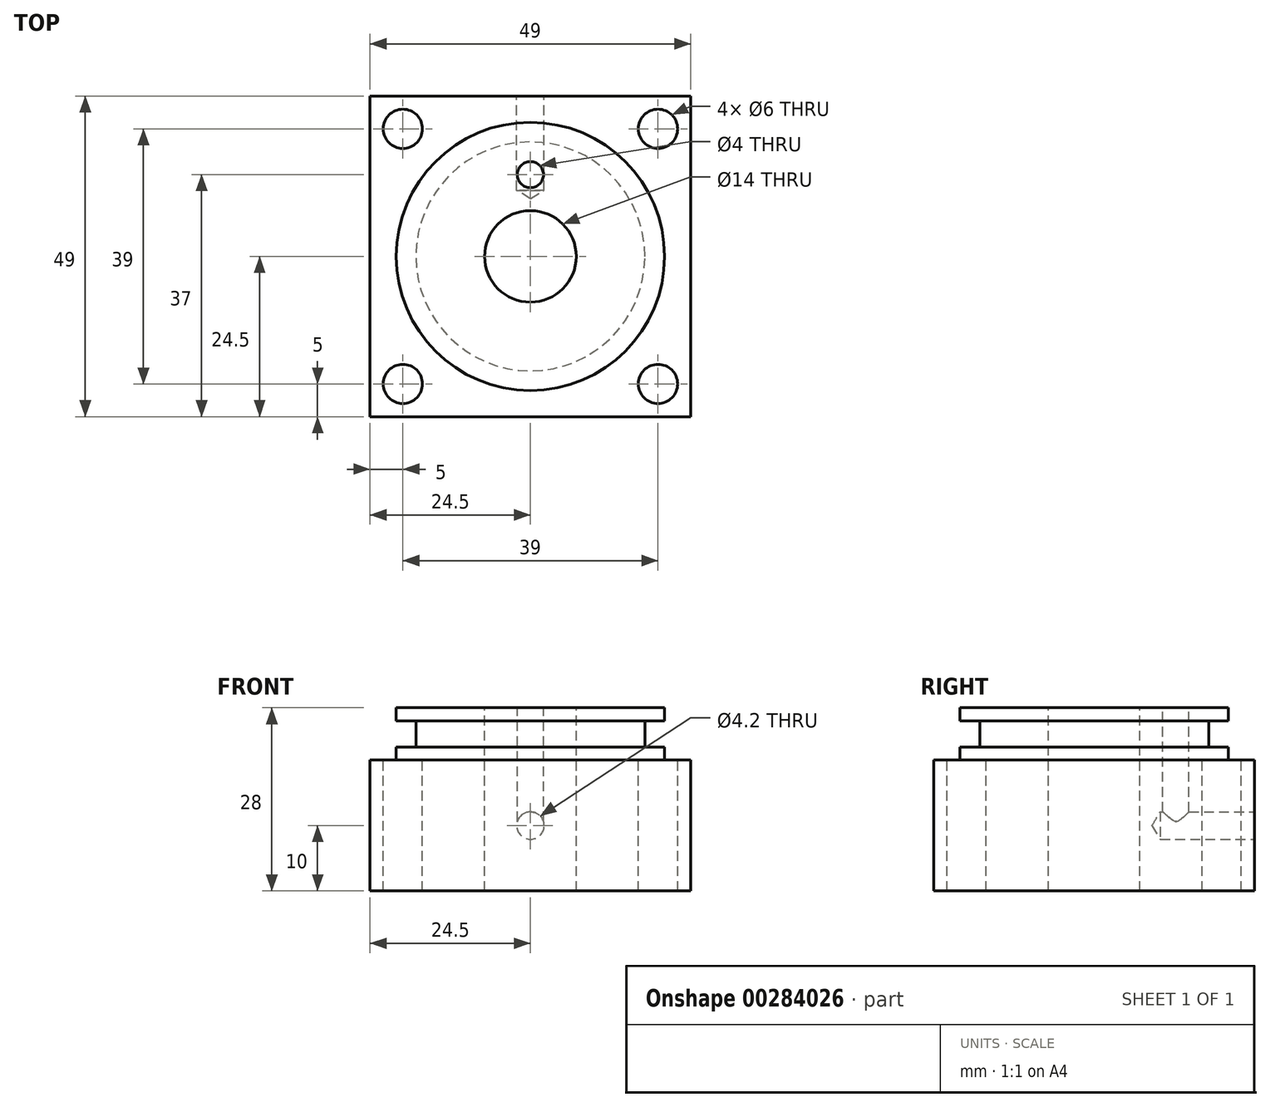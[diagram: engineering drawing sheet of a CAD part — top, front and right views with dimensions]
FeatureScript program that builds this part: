
annotation { "Feature Type Name" : "Feature", "Feature Type Description" : "" }
export const myFeature = defineFeature(function(context is Context, id is Id, definition is map)
    precondition{}
    {
        {
            var Q0;
            Q0=qCreatedBy(makeId("Top.planeOp"),FACE);
            var sketch = newSketch(context, id + "F0", { "sketchPlane" : qUnion([Q0])});
            skLineSegment(sketch, "E0.bottom", {"start": v(24.5, -24.5) * mm, "end": v(-24.5, -24.5) * mm});
            skLineSegment(sketch, "E0.top", {"start": v(24.5, 24.5) * mm, "end": v(-24.5, 24.5) * mm});
            skLineSegment(sketch, "E0.left", {"start": v(24.5, -24.5) * mm, "end": v(24.5, 24.5) * mm});
            skLineSegment(sketch, "E0.right", {"start": v(-24.5, -24.5) * mm, "end": v(-24.5, 24.5) * mm});
            skPoint(sketch, "E0.middle", {"position": v(0, 0) * mm});
            skSolve(sketch);
        }
        {
            var Q0;
            Q0 = qSketchRegion(id + "F0", true);
            extrude(context, id + "F1", {"entities" : qUnion([Q0]), "depth" : 20 * mm});
        }
        {
            var Q0;
            Q0=makeQuery(id+"F1.opExtrude","CAP_FACE",FACE,{"disambiguationData":[OSD([sQuery(id+"F0.wireOp",EDGE,"E0.bottom"),sQuery(id+"F0.wireOp",EDGE,"E0.top"),sQuery(id+"F0.wireOp",EDGE,"E0.left"),sQuery(id+"F0.wireOp",EDGE,"E0.right")])],"isStart":false});
            var sketch = newSketch(context, id + "F2", { "sketchPlane" : qUnion([Q0])});
            skLineSegment(sketch, "E1.bottom", {"start": v(19.5, 19.5) * mm, "end": v(-19.5, 19.5) * mm, "construction": true});
            skLineSegment(sketch, "E1.top", {"start": v(19.5, -19.5) * mm, "end": v(-19.5, -19.5) * mm, "construction": true});
            skLineSegment(sketch, "E1.left", {"start": v(19.5, 19.5) * mm, "end": v(19.5, -19.5) * mm, "construction": true});
            skLineSegment(sketch, "E1.right", {"start": v(-19.5, 19.5) * mm, "end": v(-19.5, -19.5) * mm, "construction": true});
            skPoint(sketch, "E1.middle", {"position": v(0, 0) * mm});
            skPoint(sketch, "E2", {"position": v(-19.5, -19.5) * mm});
            skPoint(sketch, "E3", {"position": v(-19.5, 19.5) * mm});
            skPoint(sketch, "E4", {"position": v(19.5, 19.5) * mm});
            skPoint(sketch, "E5", {"position": v(19.5, -19.5) * mm});
            skSolve(sketch);
        }
        {
            var Q0;
            Q0=sQuery(id+"F2.wireOp",VERTEX,"E2");
            var Q1;
            Q1=sQuery(id+"F2.wireOp",VERTEX,"E3");
            var Q2;
            Q2=sQuery(id+"F2.wireOp",VERTEX,"E4");
            var Q3;
            Q3=sQuery(id+"F2.wireOp",VERTEX,"E5");
            var Q4;
            Q4=makeQuery(id+"F1.opExtrude","SWEPT_BODY",BODY,{"disambiguationData":[OSD([sQuery(id+"F0.wireOp",EDGE,"E0.bottom"),sQuery(id+"F0.wireOp",EDGE,"E0.top"),sQuery(id+"F0.wireOp",EDGE,"E0.left"),sQuery(id+"F0.wireOp",EDGE,"E0.right")])]});
            hole(context, id + "F3", {"style" : HoleStyle.SIMPLE, "endStyle" : HoleEndStyle.THROUGH, "holeDiameter" : 6 * mm, "tappedDepth" : 12 * mm, "tapClearance" : 3, "locations" : qUnion([Q0, Q1, Q2, Q3]), "scope" : qUnion([Q4])});
        }
        {
            var Q0;
            Q0=qCreatedBy(makeId("Right.planeOp"),FACE);
            var sketch = newSketch(context, id + "F4", { "sketchPlane" : qUnion([Q0])});
            skLineSegment(sketch, "E6.0", {"start": v(-24.5, 20) * mm, "end": v(24.5, 20) * mm, "construction": true});
            skLineSegment(sketch, "E7", {"start": v(0, 20) * mm, "end": v(0, 28) * mm});
            skLineSegment(sketch, "E8", {"start": v(0, 28) * mm, "end": v(20.5, 28) * mm});
            skLineSegment(sketch, "E9", {"start": v(20.5, 28) * mm, "end": v(20.5, 26) * mm});
            skLineSegment(sketch, "E10", {"start": v(20.5, 26) * mm, "end": v(17.5, 26) * mm});
            skLineSegment(sketch, "E11", {"start": v(17.5, 26) * mm, "end": v(17.5, 22) * mm});
            skLineSegment(sketch, "E12", {"start": v(17.5, 22) * mm, "end": v(20.5, 22) * mm});
            skLineSegment(sketch, "E13", {"start": v(20.5, 22) * mm, "end": v(20.5, 20) * mm});
            skLineSegment(sketch, "E14", {"start": v(20.5, 20) * mm, "end": v(0, 20) * mm});
            skSolve(sketch);
        }
        {
            var Q0;
            Q0 = qSketchRegion(id + "F4", true);
            var Q1;
            Q1=sQuery(id+"F4.wireOp",EDGE,"E7");
            revolve(context, id + "F5", {"operationType" : NewBodyOperationType.ADD, "entities" : qUnion([Q0]), "axis" : qUnion([Q1]), "revolveType" : RevolveType.FULL});
        }
        {
            var Q0;
            Q0=makeQuery(id+"F1.opExtrude","SWEPT_FACE",FACE,{"disambiguationData":[OSD([sQuery(id+"F0.wireOp",EDGE,"E0.top")])]});
            var sketch = newSketch(context, id + "F6", { "sketchPlane" : qUnion([Q0])});
            skLineSegment(sketch, "E15.0", {"start": v(-24.5, 20) * mm, "end": v(24.5, 20) * mm, "construction": true});
            skLineSegment(sketch, "E16.0", {"start": v(-24.5, 0) * mm, "end": v(24.5, 0) * mm, "construction": true});
            skLineSegment(sketch, "E17", {"start": v(0, 20) * mm, "end": v(0, 10) * mm, "construction": true});
            skPoint(sketch, "E17.endSnap0", {"position": v(0, 20) * mm});
            skPoint(sketch, "E18", {"position": v(0, 10) * mm});
            skSolve(sketch);
        }
        {
            var Q0;
            Q0=sQuery(id+"F6.wireOp",VERTEX,"E18");
            var Q1;
            Q1=makeQuery(id+"F1.opExtrude","SWEPT_BODY",BODY,{"disambiguationData":[OSD([sQuery(id+"F0.wireOp",EDGE,"E0.bottom"),sQuery(id+"F0.wireOp",EDGE,"E0.top"),sQuery(id+"F0.wireOp",EDGE,"E0.left"),sQuery(id+"F0.wireOp",EDGE,"E0.right")])]});
            hole(context, id + "F7", {"style" : HoleStyle.SIMPLE, "endStyle" : HoleEndStyle.BLIND, "standardTappedOrClearance" : lookupTablePath({ "standard" : "ISO", "engagement" : "75%", "pitch" : "0.8 mm", "size" : "M5", "type" : "Tapped" }), "standardBlindInLast" : lookupTablePath({ "standard" : "ISO", "engagement" : "75%", "pitch" : "0.8 mm", "size" : "M5", "type" : "Tapped" }), "holeDiameter" : 4.2 * mm, "showTappedDepth" : true, "holeDepth" : 14.4 * mm, "tappedDepth" : 12 * mm, "tapClearance" : 3, "locations" : qUnion([Q0]), "scope" : qUnion([Q1]), "majorDiameter" : 5 * mm});
        }
        {
            var Q0;
            Q0=makeQuery(id+"F5.opRevolve","SWEPT_FACE",FACE,{"disambiguationData":[OSD([sQuery(id+"F4.wireOp",EDGE,"E8")])]});
            var sketch = newSketch(context, id + "F8", { "sketchPlane" : qUnion([Q0])});
            skLineSegment(sketch, "E19", {"start": v(0, 0) * mm, "end": v(0, 12.5) * mm, "construction": true});
            skPoint(sketch, "E20", {"position": v(0, 12.5) * mm});
            skSolve(sketch);
        }
        {
            var Q0;
            Q0=sQuery(id+"F8.wireOp",VERTEX,"E20");
            var Q1;
            Q1=makeQuery(id+"F1.opExtrude","SWEPT_BODY",BODY,{"disambiguationData":[OSD([sQuery(id+"F0.wireOp",EDGE,"E0.bottom"),sQuery(id+"F0.wireOp",EDGE,"E0.top"),sQuery(id+"F0.wireOp",EDGE,"E0.left"),sQuery(id+"F0.wireOp",EDGE,"E0.right")])]});
            hole(context, id + "F9", {"style" : HoleStyle.SIMPLE, "endStyle" : HoleEndStyle.BLIND, "holeDiameter" : 4 * mm, "holeDepth" : 18 * mm, "tappedDepth" : 12 * mm, "tapClearance" : 3, "locations" : qUnion([Q0]), "scope" : qUnion([Q1])});
        }
        {
            var Q0;
            Q0=makeQuery(id+"F5.opRevolve","SWEPT_FACE",FACE,{"disambiguationData":[OSD([sQuery(id+"F4.wireOp",EDGE,"E8")])]});
            var sketch = newSketch(context, id + "F10", { "sketchPlane" : qUnion([Q0])});
            skCircle(sketch, "E21.0", {"center": v(0, 0) * mm, "radius": 20.5 * mm, "construction": true});
            skSolve(sketch);
        }
        {
            var Q0;
            Q0=sQuery(id+"F10.wireOp",VERTEX,"E21.0.center");
            var Q1;
            Q1=makeQuery(id+"F1.opExtrude","SWEPT_BODY",BODY,{"disambiguationData":[OSD([sQuery(id+"F0.wireOp",EDGE,"E0.bottom"),sQuery(id+"F0.wireOp",EDGE,"E0.top"),sQuery(id+"F0.wireOp",EDGE,"E0.left"),sQuery(id+"F0.wireOp",EDGE,"E0.right")])]});
            hole(context, id + "F11", {"style" : HoleStyle.SIMPLE, "endStyle" : HoleEndStyle.THROUGH, "holeDiameter" : 14 * mm, "tappedDepth" : 12 * mm, "tapClearance" : 3, "locations" : qUnion([Q0]), "scope" : qUnion([Q1])});
        }
    });
